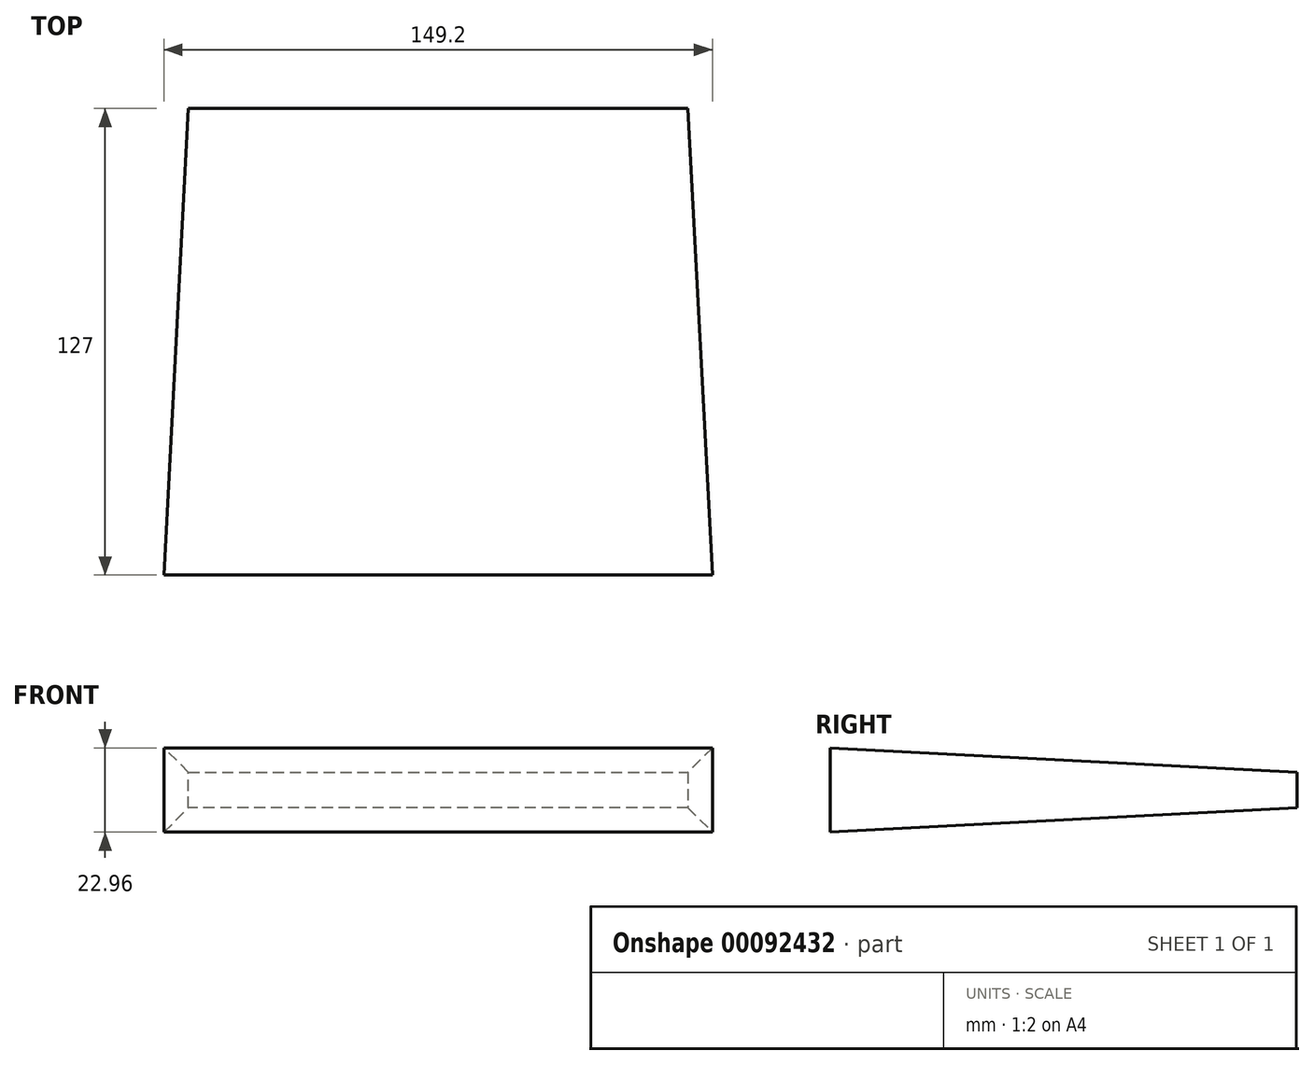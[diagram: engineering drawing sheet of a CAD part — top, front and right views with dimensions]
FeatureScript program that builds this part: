
annotation { "Feature Type Name" : "Feature", "Feature Type Description" : "" }
export const myFeature = defineFeature(function(context is Context, id is Id, definition is map)
    precondition{}
    {
        {
            var Q0;
            Q0=qCreatedBy(makeId("Front.planeOp"),FACE);
            var sketch = newSketch(context, id + "F0", { "sketchPlane" : qUnion([Q0])});
            skLineSegment(sketch, "E0.bottom", {"start": v(-112.2, -22.58) * mm, "end": v(23.7, -22.58) * mm});
            skLineSegment(sketch, "E0.top", {"start": v(-112.2, -32.22) * mm, "end": v(23.7, -32.22) * mm});
            skLineSegment(sketch, "E0.left", {"start": v(-112.2, -22.58) * mm, "end": v(-112.2, -32.22) * mm});
            skLineSegment(sketch, "E0.right", {"start": v(23.7, -22.58) * mm, "end": v(23.7, -32.22) * mm});
            skSolve(sketch);
        }
        {
            var Q0;
            Q0=makeQuery(id+"F0.imprint","IMPRINT",FACE,{"disambiguationData":[TD([[makeQuery(id+"F0.imprint","IMPRINT",EDGE,{"derivedFrom":sQuery(id+"F0.wireOp",EDGE,"E0.bottom")}),-1.0]])]});
            extrude(context, id + "F1", {"entities" : qUnion([Q0]), "depth" : 127 * mm, "hasDraft" : true, "draftAngle" : 3 * degree});
        }
    });
